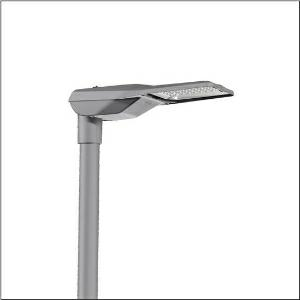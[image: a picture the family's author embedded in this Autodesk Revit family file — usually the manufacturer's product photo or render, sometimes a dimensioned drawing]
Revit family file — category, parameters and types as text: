
# Revit family: streetlight_sl_21_iq_mini___p0_5a_5xe2v31v08jb_ab6f
name_source: partatom
category: Lighting Fixtures
units: mm (PartAtom-declared; Revit-internal decimal feet)

## family parameters
Cut with Voids When Loaded = No
Host = Face
Light Source = No
Part Type = Normal
Room Calculation Point = No
Round Connector Dimension = Use Diameter
Shared = No

## types (1)
- --- (1 x LED, 11020 lm, 72.5 W, 3000K)
    Apparent Load = 73 VA
    CIE Flux Codes = 37 73 96 100 100
    Color Rendering = 70
    Color Temperature = 3000K
    Default Elevation = 1800 mm
    Description = Streetlight SL 21 iQ mini, mast luminaire, primary light control with lens, of PMMA, primary optical cover: cover, of toughened safety glass, transparent, light distribution: P0.5a, light emission: direct distribution, primary light characteristic: asymmetric, installation type: post-top, side-entry, LED, High Power LED, rated luminous flux: 11.020lm, luminous efficacy: 152lm/W, light colour: 730, colour temperature: 3000K, control gear: iQ-Street Remote, D4i with power reduction, control: pre-setting: logarithmic dimming characteristic, Street-Remote, Auto-Match, Temp-Guard, Lumen-Switch, Night-Set, Smart-Wire, Light-Fading, Desk-Remote (wireless, voltage-free reading and setting of iQ features in the workshop via application-optimized NFC function/RFID function), optimised constant luminous flux control (CLO 2.0), mains connection: 220..240V, AC, 50/60Hz, start of lifetime: 73W, end of service life: 76W, reduction: 33W, luminaire housing, of diecast aluminium, powder-coated, Siteco® metallic grey (DB 702S), corrosivity category C5 mid according to DIN EN ISO 12944, please order mast flange separately, inclination adjustable: 0°, 5°, 10°, 15°, sealing non-destructively replaceable, multi-level sealing system, length: 628mm, width: 235mm, height: 110mm, mast flange for spigot size: 42mm (side-entry): 5XC10008XM4, 60/48mm (side-entry/post-top): 5XC10108XM2, 76/60mm (side-entry/post-top): 5XC10108XM1, mounting height: 4..8m, Smart Interface above, protection rating (complete): IP66, insulation class (complete): insulation class II (safety insulation), certification: CE, ENEC, ENEC+, VDE, impact resistance: IK10, permissible operating ambient temperature for outdoor applications: -40..+50°C, standard-compliant lighting for roads and squares, packaging unit: 1 piece

Light Distribution: P0.5a
    Height = 110 mm
    Lamp = 1 x LED
    Lamp Light Flux = 11020 lm
    Lamp Power = 72.5 W
    Lamp count = 1
    Length = 625 mm
    Luminous efficacy = 152 lm/W
    Manufacturer = Siteco
    ModVariant = No
    Model = 5XE2V31V08JB
    Number of Poles = 1
    OnlyDefault = Yes
    Power Factor = 1
    Product Name = Streetlight SL 21 iQ mini | P0.5a
    Product group = mast luminaire | pylon top
    ProductGroupID = 6100
    Protection Class = Protection class II
    Protection Degree = IP 66
    RLX_Detail_Level = 1
    RLX_Emergency_Light_Flux = 0 lm
    RLX_Emergency_Type = 0
    RLX_Emergency_Type_DB = No
    RlxData = <blob elided: 26205 chars, md5=d3e87315>
    Socket = socket
    Standby Power = 0 W
    System Light Flux = 11020 lm
    System Power = 73 W
    Type Comments = factory setting: luminous flux: 100 % | dim-lin: 254 | 755 mA
    Type Image = l_1003515.jpg
    URL = http://relux.com
    VarID = @adj_069426
    Voltage = 0 V
    Weight = 0.00 kg
    Width = 234 mm

## geometry (parser evidence)
native form markers: Blend x4, Sweep x10
no freeform markers — native parametric forms only
